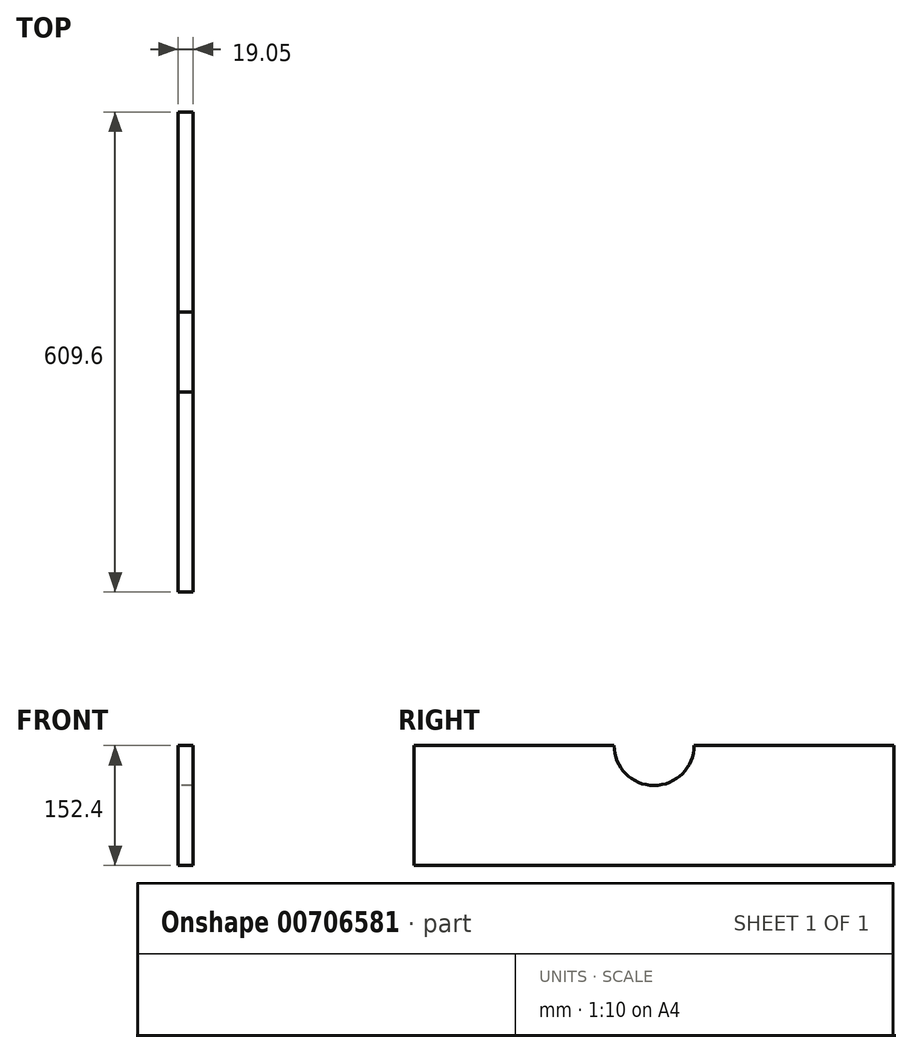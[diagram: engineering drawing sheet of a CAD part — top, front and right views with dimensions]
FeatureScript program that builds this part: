
annotation { "Feature Type Name" : "Feature", "Feature Type Description" : "" }
export const myFeature = defineFeature(function(context is Context, id is Id, definition is map)
    precondition{}
    {
        {
            var Q0;
            Q0=qCreatedBy(makeId("Right.planeOp"),FACE);
            var sketch = newSketch(context, id + "F0", { "sketchPlane" : qUnion([Q0])});
            skLineSegment(sketch, "E0.bottom", {"start": v(304.8, 76.2) * mm, "end": v(-304.8, 76.2) * mm});
            skLineSegment(sketch, "E0.top", {"start": v(304.8, -76.2) * mm, "end": v(-304.8, -76.2) * mm});
            skLineSegment(sketch, "E0.left", {"start": v(304.8, 76.2) * mm, "end": v(304.8, -76.2) * mm});
            skLineSegment(sketch, "E0.right", {"start": v(-304.8, 76.2) * mm, "end": v(-304.8, -76.2) * mm});
            skPoint(sketch, "E0.middle", {"position": v(0, 0) * mm});
            skCircle(sketch, "E1", {"center": v(0, 76.2) * mm, "radius": 50.8 * mm});
            skSolve(sketch);
        }
        {
            var Q0;
            Q0=makeQuery(id+"F0.imprint","IMPRINT",FACE,{"disambiguationData":[TD([[makeQuery(id+"F0.imprint","IMPRINT",EDGE,{"derivedFrom":sQuery(id+"F0.wireOp",EDGE,"E0.top")}),-1.0]])]});
            extrude(context, id + "F1", {"entities" : qUnion([Q0]), "depth" : 19.05 * mm, "offsetDistance" : 25.4 * mm});
        }
    });
